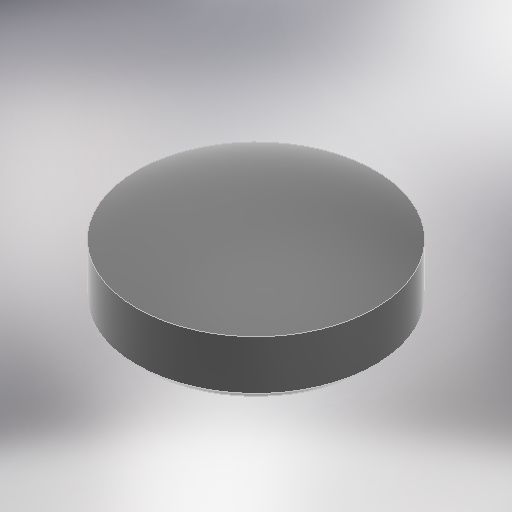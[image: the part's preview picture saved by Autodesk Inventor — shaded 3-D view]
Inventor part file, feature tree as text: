
AUTODESK INVENTOR PART (.ipt)
format: ipt  version: 2025 (Build 290162000, 162)  size: 331,264 bytes
history: native  units: mm
features: revolve x1, thread x1, sketch x1
ambient origin geometry x8: Origin, YZ Plane, XZ Plane, XY Plane, X Axis, Y Axis, Z Axis, Center Point
bodies: 实体1 (feature_tree)
feature tree (3):
  revolve  "旋转1"  Angle=45.0deg
  thread  "螺纹1"  [1 undecoded]
  sketch  "草图2"  dims[d1=48.0mm d2=12.0mm d3=5.0mm d4=22.0mm d0=45.0deg d5=2.0mm d6=27.5mm d7=20.0mm d8=60.0mm d9=360.0deg d10=1.0mm d11=1.0mm d12=2.0mm d13=2.0mm d14=7.0mm d15=18.45mm d16=24.0mm d17=20.0mm d18=0.0mm]
note: 1 required parameter value undecoded (feature->parameter linkage not recoverable at this tier; creation-order binding heuristic only, values carry confidence <= 0.55)
